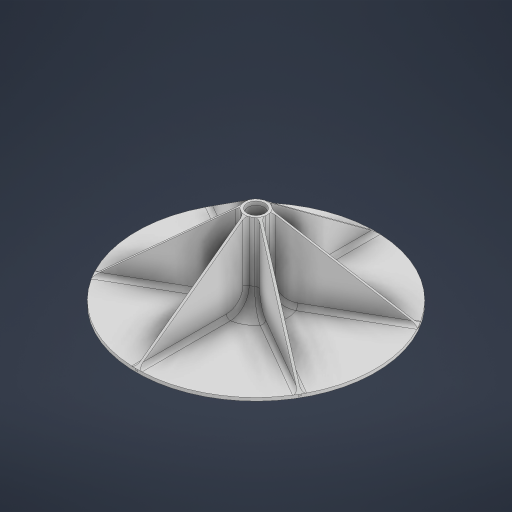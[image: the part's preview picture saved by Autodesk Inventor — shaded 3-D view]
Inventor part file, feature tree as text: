
AUTODESK INVENTOR PART (.ipt)
format: ipt  version: 2023 (Build 270158000, 158)  size: 405,504 bytes
history: native  units: mm
features: fillet x2, sketch x2, revolve x1, extrude x1, pattern_circular x1, chamfer x1, projected_geometry x1
ambient origin geometry x8: Origin, YZ Plane, XZ Plane, XY Plane, X Axis, Y Axis, Z Axis, Center Point
bodies: Solid1 (feature_tree)
feature tree (9):
  revolve  "Revolution1"  [1 undecoded]
  fillet  "Fillet1"  Radius=10.2mm
  extrude  "Extrusion1"  TaperAngle=90.0deg  [1 undecoded]
  fillet  "Fillet2"  Radius=25.0mm
  pattern_circular  "Circular Pattern1"  Count=10  [1 undecoded]
  chamfer  "Chamfer1"  Distance=3.0mm
  sketch  "Sketch1"  dims[d0=4.0mm d1=150.0mm d2=10.2mm]
  sketch  "Sketch2"  dims[d3=4.0mm d4=90.0deg d5=25.0mm d6=100.0mm d7=3.0mm d8=0.0mm d9=5.0mm d10=60.0mm d11=360.0deg d13=1.0mm d14=4.0mm d15=45.0deg]
  projected_geometry  "Project Cut Edges1"
note: 3 required parameter values undecoded (feature->parameter linkage not recoverable at this tier; creation-order binding heuristic only, values carry confidence <= 0.55)